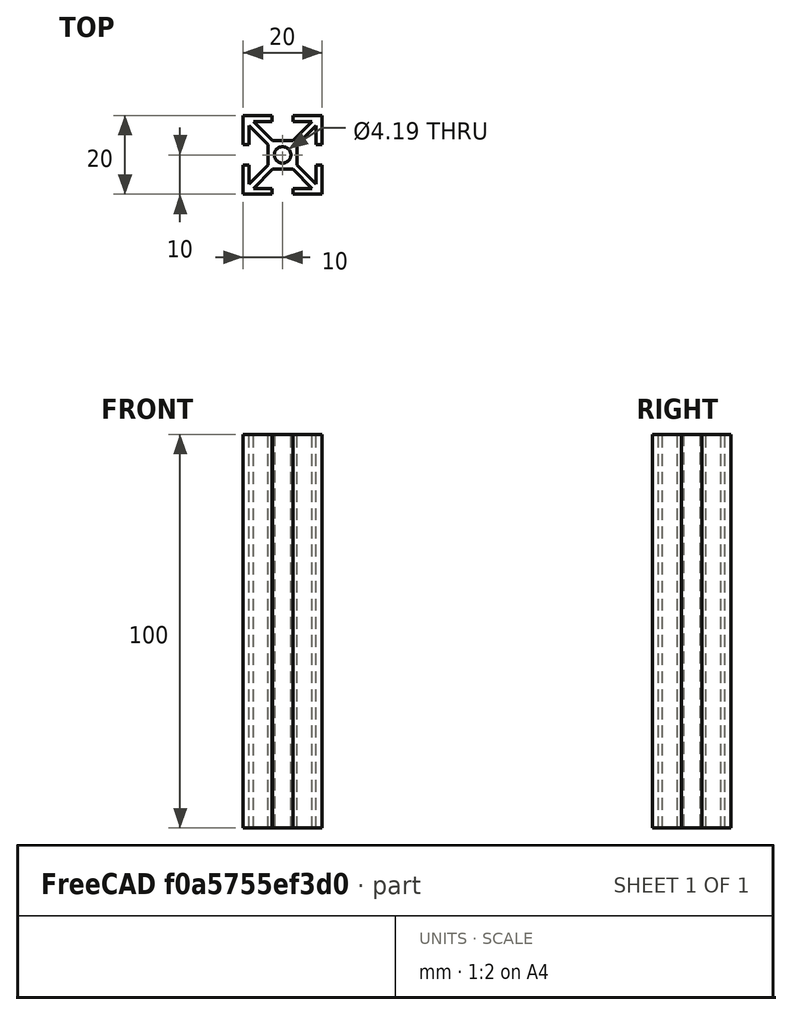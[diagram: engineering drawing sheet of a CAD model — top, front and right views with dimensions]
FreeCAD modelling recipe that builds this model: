
FCSTD DOCUMENT  (FreeCAD 0.15R4671 (Git))
Label: 20series-1x1_100mm
License: All rights reserved
LicenseURL: http://en.wikipedia.org/wiki/All_rights_reserved
objects: Sketcher::SketchObject×1, Part::Extrusion×1
note: 2 computed .brp shape members not serialized (recipe doc carries the construction recipe); baked Part::Feature solids carry a one-line shape summary decoded from their .brp

FEATURE [Sketcher::SketchObject] Sketch  label="20seriesProfile"
  sketch-geometry (93):
    g0: LineSegment [constr] StartX=0 StartY=0 StartZ=0 EndX=20 EndY=0 EndZ=0
    g1: LineSegment [constr] StartX=20 StartY=0 StartZ=0 EndX=20 EndY=20 EndZ=0
    g2: LineSegment [constr] StartX=20 StartY=20 StartZ=0 EndX=0 EndY=20 EndZ=0
    g3: LineSegment [constr] StartX=0 StartY=20 StartZ=0 EndX=0 EndY=0 EndZ=0
    g4: LineSegment [constr] StartX=0 StartY=0 StartZ=0 EndX=20 EndY=20 EndZ=0
    g5: LineSegment [constr] StartX=0 StartY=20 StartZ=0 EndX=20 EndY=0 EndZ=0
    g6: GeomPoint [constr] X=0 Y=10 Z=0
    g7: GeomPoint [constr] X=20 Y=10 Z=0
    g8: GeomPoint [constr] X=10 Y=20 Z=0
    g9: GeomPoint [constr] X=10 Y=0 Z=0
    g10: LineSegment [constr] StartX=0 StartY=10 StartZ=0 EndX=20 EndY=10 EndZ=0
    g11: LineSegment [constr] StartX=10 StartY=20 StartZ=0 EndX=10 EndY=0 EndZ=0
    g12: GeomPoint [constr] X=10 Y=10 Z=0
    g13: Circle CenterX=10 CenterY=10 CenterZ=0 NormalX=0 NormalY=0 NormalZ=1 Radius=2.095
    g14: LineSegment StartX=6.34 StartY=6.34 StartZ=0 EndX=13.66 EndY=6.34 EndZ=0
    g15: LineSegment StartX=13.66 StartY=6.34 StartZ=0 EndX=13.66 EndY=13.66 EndZ=0
    g16: LineSegment StartX=13.66 StartY=13.66 StartZ=0 EndX=6.34 EndY=13.66 EndZ=0
    g17: LineSegment StartX=6.34 StartY=13.66 StartZ=0 EndX=6.34 EndY=6.34 EndZ=0
    g18: LineSegment [constr] StartX=1.5 StartY=1.5 StartZ=0 EndX=18.5 EndY=1.5 EndZ=0
    g19: LineSegment [constr] StartX=18.5 StartY=1.5 StartZ=0 EndX=18.5 EndY=18.5 EndZ=0
    g20: LineSegment [constr] StartX=18.5 StartY=18.5 StartZ=0 EndX=1.5 EndY=18.5 EndZ=0
    g21: LineSegment [constr] StartX=1.5 StartY=18.5 StartZ=0 EndX=1.5 EndY=1.5 EndZ=0
    g22: LineSegment [constr] StartX=1.5 StartY=1.5 StartZ=0 EndX=0 EndY=1.5 EndZ=0
    g23: LineSegment [constr] StartX=2.56066 StartY=1.5 StartZ=0 EndX=7.40066 EndY=6.34 EndZ=0
    g24: LineSegment [constr] StartX=6.34 StartY=7.40066 StartZ=0 EndX=1.5 EndY=2.56066 EndZ=0
    g25: LineSegment [constr] StartX=1.5 StartY=2.56066 StartZ=0 EndX=2.56066 EndY=1.5 EndZ=0
    g26: LineSegment [constr] StartX=17.4393 StartY=1.5 StartZ=0 EndX=12.5993 EndY=6.34 EndZ=0
    g27: LineSegment [constr] StartX=13.66 StartY=7.40066 StartZ=0 EndX=18.5 EndY=2.56066 EndZ=0
    g28: LineSegment [constr] StartX=2.56066 StartY=18.5 StartZ=0 EndX=7.40066 EndY=13.66 EndZ=0
    g29: LineSegment [constr] StartX=1.5 StartY=17.4393 StartZ=0 EndX=6.34 EndY=12.5993 EndZ=0
    g30: LineSegment [constr] StartX=2.56066 StartY=18.5 StartZ=0 EndX=1.5 EndY=17.4393 EndZ=0
    g31: LineSegment [constr] StartX=18.5 StartY=2.56066 StartZ=0 EndX=17.4393 EndY=1.5 EndZ=0
    g32: LineSegment [constr] StartX=17.4393 StartY=18.5 StartZ=0 EndX=12.5993 EndY=13.66 EndZ=0
    g33: LineSegment [constr] StartX=13.66 StartY=12.5993 StartZ=0 EndX=18.5 EndY=17.4393 EndZ=0
    g34: LineSegment [constr] StartX=18.5 StartY=17.4393 StartZ=0 EndX=17.4393 EndY=18.5 EndZ=0
    g35: LineSegment [constr] StartX=0 StartY=7.37 StartZ=0 EndX=1.5 EndY=7.37 EndZ=0
    g36: LineSegment [constr] StartX=1.5 StartY=12.63 StartZ=0 EndX=0 EndY=12.63 EndZ=0
    g37: LineSegment [constr] StartX=0.75 StartY=12.63 StartZ=0 EndX=0.75 EndY=7.37 EndZ=0
    g38: GeomPoint [constr] X=0.75 Y=10 Z=0
    g39: LineSegment [constr] StartX=18.5 StartY=12.63 StartZ=0 EndX=20 EndY=12.63 EndZ=0
    g40: LineSegment [constr] StartX=18.5 StartY=7.37 StartZ=0 EndX=20 EndY=7.37 EndZ=0
    g41: LineSegment [constr] StartX=7.37 StartY=1.5 StartZ=0 EndX=7.37 EndY=0 EndZ=0
    g42: LineSegment [constr] StartX=12.63 StartY=1.5 StartZ=0 EndX=12.63 EndY=0 EndZ=0
    g43: LineSegment [constr] StartX=7.37 StartY=0.75 StartZ=0 EndX=12.63 EndY=0.75 EndZ=0
    g44: LineSegment [constr] StartX=7.37 StartY=20 StartZ=0 EndX=7.37 EndY=18.5 EndZ=0
    g45: LineSegment [constr] StartX=12.63 StartY=20 StartZ=0 EndX=12.63 EndY=18.5 EndZ=0
    g46: GeomPoint [constr] X=7.37 Y=19.25 Z=0
    g47: LineSegment [constr] StartX=7.37 StartY=19.25 StartZ=0 EndX=12.63 EndY=19.25 EndZ=0
    g48: GeomPoint [constr] X=19.25 Y=12.63 Z=0
    g49: LineSegment [constr] StartX=19.25 StartY=12.63 StartZ=0 EndX=19.25 EndY=7.37 EndZ=0
    g50: GeomPoint [constr] X=19.25 Y=10 Z=0
    g51: GeomPoint [constr] X=10 Y=19.25 Z=0
    g52: GeomPoint [constr] X=10 Y=0.75 Z=0
    g53: LineSegment StartX=0 StartY=7.37 StartZ=0 EndX=0 EndY=0 EndZ=0
    g54: LineSegment StartX=0 StartY=0 StartZ=0 EndX=7.37 EndY=0 EndZ=0
    g55: LineSegment StartX=7.37 StartY=0 StartZ=0 EndX=7.37 EndY=1.5 EndZ=0
    g56: LineSegment StartX=7.37 StartY=1.5 StartZ=0 EndX=2.56066 EndY=1.5 EndZ=0
    g57: LineSegment StartX=2.56066 StartY=1.5 StartZ=0 EndX=7.40066 EndY=6.34 EndZ=0
    g58: LineSegment StartX=7.40066 StartY=6.34 StartZ=0 EndX=6.34 EndY=6.34 EndZ=0
    g59: LineSegment StartX=6.34 StartY=6.34 StartZ=0 EndX=6.34 EndY=7.40066 EndZ=0
    g60: LineSegment StartX=6.34 StartY=7.40066 StartZ=0 EndX=1.5 EndY=2.56066 EndZ=0
    g61: LineSegment StartX=1.5 StartY=2.56066 StartZ=0 EndX=1.5 EndY=7.37 EndZ=0
    g62: LineSegment StartX=1.5 StartY=7.37 StartZ=0 EndX=0 EndY=7.37 EndZ=0
    g63: LineSegment StartX=20 StartY=7.37 StartZ=0 EndX=20 EndY=0 EndZ=0
    g64: LineSegment StartX=20 StartY=0 StartZ=0 EndX=12.63 EndY=0 EndZ=0
    g65: LineSegment StartX=12.63 StartY=0 StartZ=0 EndX=12.63 EndY=1.5 EndZ=0
    g66: LineSegment StartX=12.63 StartY=1.5 StartZ=0 EndX=17.4393 EndY=1.5 EndZ=0
    g67: LineSegment StartX=17.4393 StartY=1.5 StartZ=0 EndX=12.5993 EndY=6.34 EndZ=0
    g68: LineSegment StartX=12.5993 StartY=6.34 StartZ=0 EndX=13.66 EndY=6.34 EndZ=0
    g69: LineSegment StartX=13.66 StartY=6.34 StartZ=0 EndX=13.66 EndY=7.40066 EndZ=0
    g70: LineSegment StartX=13.66 StartY=7.40066 StartZ=0 EndX=18.5 EndY=2.56066 EndZ=0
    g71: LineSegment StartX=18.5 StartY=2.56066 StartZ=0 EndX=18.5 EndY=7.37 EndZ=0
    g72: LineSegment StartX=18.5 StartY=7.37 StartZ=0 EndX=20 EndY=7.37 EndZ=0
    g73: LineSegment StartX=1.5 StartY=12.63 StartZ=0 EndX=1.5 EndY=17.4393 EndZ=0
    g74: LineSegment StartX=1.5 StartY=17.4393 StartZ=0 EndX=6.34 EndY=12.5993 EndZ=0
    g75: LineSegment StartX=6.34 StartY=12.5993 StartZ=0 EndX=6.34 EndY=13.66 EndZ=0
    g76: LineSegment StartX=6.34 StartY=13.66 StartZ=0 EndX=7.40066 EndY=13.66 EndZ=0
    g77: LineSegment StartX=7.40066 StartY=13.66 StartZ=0 EndX=2.56066 EndY=18.5 EndZ=0
    g78: LineSegment StartX=2.56066 StartY=18.5 StartZ=0 EndX=7.37 EndY=18.5 EndZ=0
    g79: LineSegment StartX=7.37 StartY=18.5 StartZ=0 EndX=7.37 EndY=20 EndZ=0
    g80: LineSegment StartX=7.37 StartY=20 StartZ=0 EndX=0 EndY=20 EndZ=0
    g81: LineSegment StartX=0 StartY=20 StartZ=0 EndX=0 EndY=12.63 EndZ=0
    g82: LineSegment StartX=0 StartY=12.63 StartZ=0 EndX=1.5 EndY=12.63 EndZ=0
    g83: LineSegment StartX=20 StartY=12.63 StartZ=0 EndX=20 EndY=20 EndZ=0
    g84: LineSegment StartX=20 StartY=20 StartZ=0 EndX=12.63 EndY=20 EndZ=0
    g85: LineSegment StartX=12.63 StartY=20 StartZ=0 EndX=12.63 EndY=18.5 EndZ=0
    g86: LineSegment StartX=12.63 StartY=18.5 StartZ=0 EndX=17.4393 EndY=18.5 EndZ=0
    g87: LineSegment StartX=17.4393 StartY=18.5 StartZ=0 EndX=12.5993 EndY=13.66 EndZ=0
    g88: LineSegment StartX=12.5993 StartY=13.66 StartZ=0 EndX=13.66 EndY=13.66 EndZ=0
    g89: LineSegment StartX=13.66 StartY=13.66 StartZ=0 EndX=13.66 EndY=12.5993 EndZ=0
    g90: LineSegment StartX=13.66 StartY=12.5993 StartZ=0 EndX=18.5 EndY=17.4393 EndZ=0
    g91: LineSegment StartX=18.5 StartY=17.4393 StartZ=0 EndX=18.5 EndY=12.63 EndZ=0
    g92: LineSegment StartX=18.5 StartY=12.63 StartZ=0 EndX=20 EndY=12.63 EndZ=0
  constraints (233):
    c: Coincident(g0,g1)
    c: Coincident(g1,g2)
    c: Coincident(g2,g3)
    c: Coincident(g3,g0)
    c: Horizontal(g0)
    c: Vertical(g1)
    c: Coincident(g0,g-1)
    c: Equal(g0,g3)
    c: DistanceX(g0) = 20
    c: Coincident(g4,g-1)
    c: Coincident(g4,g1)
    c: Coincident(g5,g2)
    c: Coincident(g5,g0)
    c: PointOnObject(g8,g2)
    c: Symmetric(g0,g0,g9)
    c: Symmetric(g1,g1,g7)
    c: Symmetric(g2,g2,g8)
    c: Symmetric(g3,g3,g6)
    c: Horizontal(g10)
    c: Coincident(g10,g7)
    c: Coincident(g10,g6)
    c: PointOnObject(g11,g2)
    c: PointOnObject(g11,g0)
    c: Vertical(g11)
    c: Coincident(g11,g9)
    c: PointOnObject(g12,g11)
    c: Symmetric(g10,g10,g12)
    c: Radius(g13) = 2.095
    c: Coincident(g13,g12)
    c: Coincident(g14,g15)
    c: Coincident(g15,g16)
    c: Coincident(g16,g17)
    c: Coincident(g17,g14)
    c: Horizontal(g14)
    c: Horizontal(g16)
    c: Vertical(g15)
    c: Vertical(g17)
    c: PointOnObject(g14,g4)
    c: PointOnObject(g15,g4)
    c: PointOnObject(g14,g5)
    c: DistanceX(g14) = 7.32
    c: Coincident(g18,g19)
    c: Coincident(g19,g20)
    c: Coincident(g20,g21)
    c: Coincident(g21,g18)
    c: Horizontal(g18)
    c: Vertical(g21)
    c: PointOnObject(g18,g4)
    c: PointOnObject(g19,g4)
    c: Equal(g21,g18)
    c: PointOnObject(g20,g5)
    c: Coincident(g22,g18)
    c: PointOnObject(g22,g3)
    c: Horizontal(g22)
    c: DistanceX(g22) = -1.5
    c: PointOnObject(g23,g14)
    c: Parallel(g23,g4)
    c: PointOnObject(g24,g17)
    c: PointOnObject(g24,g21)
    c: Parallel(g24,g4)
    c: PointOnObject(g23,g18)
    c: Coincident(g25,g24)
    c: Coincident(g25,g23)
    c: Perpendicular(g4,g25)
    c: Distance(g25) = 1.5
    c: PointOnObject(g26,g18)
    c: PointOnObject(g26,g14)
    c: PointOnObject(g27,g15)
    c: PointOnObject(g27,g19)
    c: PointOnObject(g28,g20)
    c: PointOnObject(g28,g16)
    c: PointOnObject(g29,g21)
    c: PointOnObject(g29,g17)
    c: Parallel(g29,g28)
    c: Parallel(g28,g27)
    c: Parallel(g27,g26)
    c: Parallel(g26,g5)
    c: Coincident(g30,g28)
    c: Coincident(g29,g30)
    c: Coincident(g31,g27)
    c: Coincident(g31,g26)
    c: Perpendicular(g5,g31)
    c: Perpendicular(g5,g30)
    c: Equal(g31,g30)
    c: Equal(g30,g25)
    c: PointOnObject(g32,g20)
    c: PointOnObject(g32,g16)
    c: PointOnObject(g33,g15)
    c: PointOnObject(g33,g19)
    c: Coincident(g34,g33)
    c: Parallel(g33,g32)
    c: Parallel(g32,g4)
    c: Coincident(g34,g32)
    c: Perpendicular(g4,g34)
    c: Equal(g34,g25)
    c: PointOnObject(g35,g3)
    c: PointOnObject(g35,g21)
    c: Horizontal(g35)
    c: PointOnObject(g36,g21)
    c: Horizontal(g36)
    c: Vertical(g37)
    c: Symmetric(g37,g37,g38)
    c: PointOnObject(g38,g10)
    c: PointOnObject(g37,g36)
    c: PointOnObject(g37,g35)
    c: Symmetric(g36,g36,g37)
    c: PointOnObject(g36,g3)
    c: DistanceY(g36,g35) = -5.26
    c: PointOnObject(g39,g19)
    c: PointOnObject(g39,g1)
    c: Horizontal(g39)
    c: PointOnObject(g40,g19)
    c: PointOnObject(g40,g1)
    c: Horizontal(g40)
    c: PointOnObject(g41,g18)
    c: PointOnObject(g41,g0)
    c: Vertical(g41)
    c: PointOnObject(g42,g18)
    c: PointOnObject(g42,g0)
    c: Vertical(g42)
    c: PointOnObject(g43,g41)
    c: PointOnObject(g43,g42)
    c: Horizontal(g43)
    c: Symmetric(g41,g41,g43)
    c: PointOnObject(g44,g2)
    c: PointOnObject(g44,g20)
    c: Vertical(g44)
    c: Vertical(g45)
    c: PointOnObject(g46,g44)
    c: Coincident(g47,g46)
    c: PointOnObject(g47,g45)
    c: Horizontal(g47)
    c: Symmetric(g44,g44,g46)
    c: PointOnObject(g48,g39)
    c: Coincident(g49,g48)
    c: PointOnObject(g49,g40)
    c: Vertical(g49)
    c: Symmetric(g39,g39,g48)
    c: PointOnObject(g50,g49)
    c: PointOnObject(g50,g10)
    c: PointOnObject(g51,g47)
    c: Symmetric(g47,g47,g51)
    c: PointOnObject(g51,g11)
    c: Equal(g47,g49)
    c: Equal(g49,g43)
    c: PointOnObject(g52,g43)
    c: Symmetric(g43,g43,g52)
    c: PointOnObject(g52,g11)
    c: Equal(g37,g47)
    c: Symmetric(g49,g49,g50)
    c: PointOnObject(g45,g2)
    c: PointOnObject(g45,g20)
    c: Coincident(g35,g53)
    c: Coincident(g53,g-1)
    c: Coincident(g53,g54)
    c: Coincident(g54,g41)
    c: Coincident(g54,g55)
    c: Coincident(g55,g41)
    c: Coincident(g55,g56)
    c: Coincident(g56,g23)
    c: Coincident(g56,g57)
    c: Coincident(g57,g23)
    c: Coincident(g57,g58)
    c: Coincident(g58,g14)
    c: Coincident(g58,g59)
    c: Coincident(g59,g24)
    c: Coincident(g59,g60)
    c: Coincident(g60,g24)
    c: Coincident(g60,g61)
    c: Coincident(g61,g35)
    c: Coincident(g61,g62)
    c: Coincident(g62,g53)
    c: Coincident(g40,g63)
    c: Coincident(g63,g0)
    c: Coincident(g63,g64)
    c: Coincident(g64,g42)
    c: Coincident(g64,g65)
    c: Coincident(g65,g42)
    c: Coincident(g65,g66)
    c: Coincident(g66,g26)
    c: Coincident(g66,g67)
    c: Coincident(g67,g26)
    c: Coincident(g67,g68)
    c: Coincident(g68,g14)
    c: Coincident(g68,g69)
    c: Coincident(g69,g27)
    c: Coincident(g69,g70)
    c: Coincident(g70,g27)
    c: Coincident(g70,g71)
    c: Coincident(g71,g40)
    c: Coincident(g71,g72)
    c: Coincident(g72,g63)
    c: Coincident(g36,g73)
    c: Coincident(g73,g29)
    c: Coincident(g73,g74)
    c: Coincident(g74,g29)
    c: Coincident(g74,g75)
    c: Coincident(g75,g16)
    c: Coincident(g75,g76)
    c: Coincident(g76,g28)
    c: Coincident(g76,g77)
    c: Coincident(g77,g28)
    c: Coincident(g77,g78)
    c: Coincident(g78,g44)
    c: Coincident(g78,g79)
    c: Coincident(g79,g44)
    c: Coincident(g79,g80)
    c: Coincident(g80,g2)
    c: Coincident(g80,g81)
    c: Coincident(g81,g36)
    c: Coincident(g81,g82)
    c: Coincident(g82,g73)
    c: Coincident(g39,g83)
    c: Coincident(g83,g1)
    c: Coincident(g83,g84)
    c: Coincident(g84,g45)
    c: Coincident(g84,g85)
    c: Coincident(g85,g45)
    c: Coincident(g85,g86)
    c: Coincident(g86,g32)
    c: Horizontal(g86)
    c: Coincident(g86,g87)
    c: Coincident(g87,g32)
    c: Coincident(g87,g88)
    c: Coincident(g88,g15)
    c: Coincident(g88,g89)
    c: Coincident(g89,g90)
    c: Coincident(g90,g33)
    c: Coincident(g90,g91)
    c: Coincident(g91,g39)
    c: Coincident(g91,g92)
    c: Coincident(g92,g83)
    c: Coincident(g89,g33)
FEATURE [Part::Extrusion] Extrude
  Base = -> Sketch
  Dir = (0,0,100)
  Solid = true
